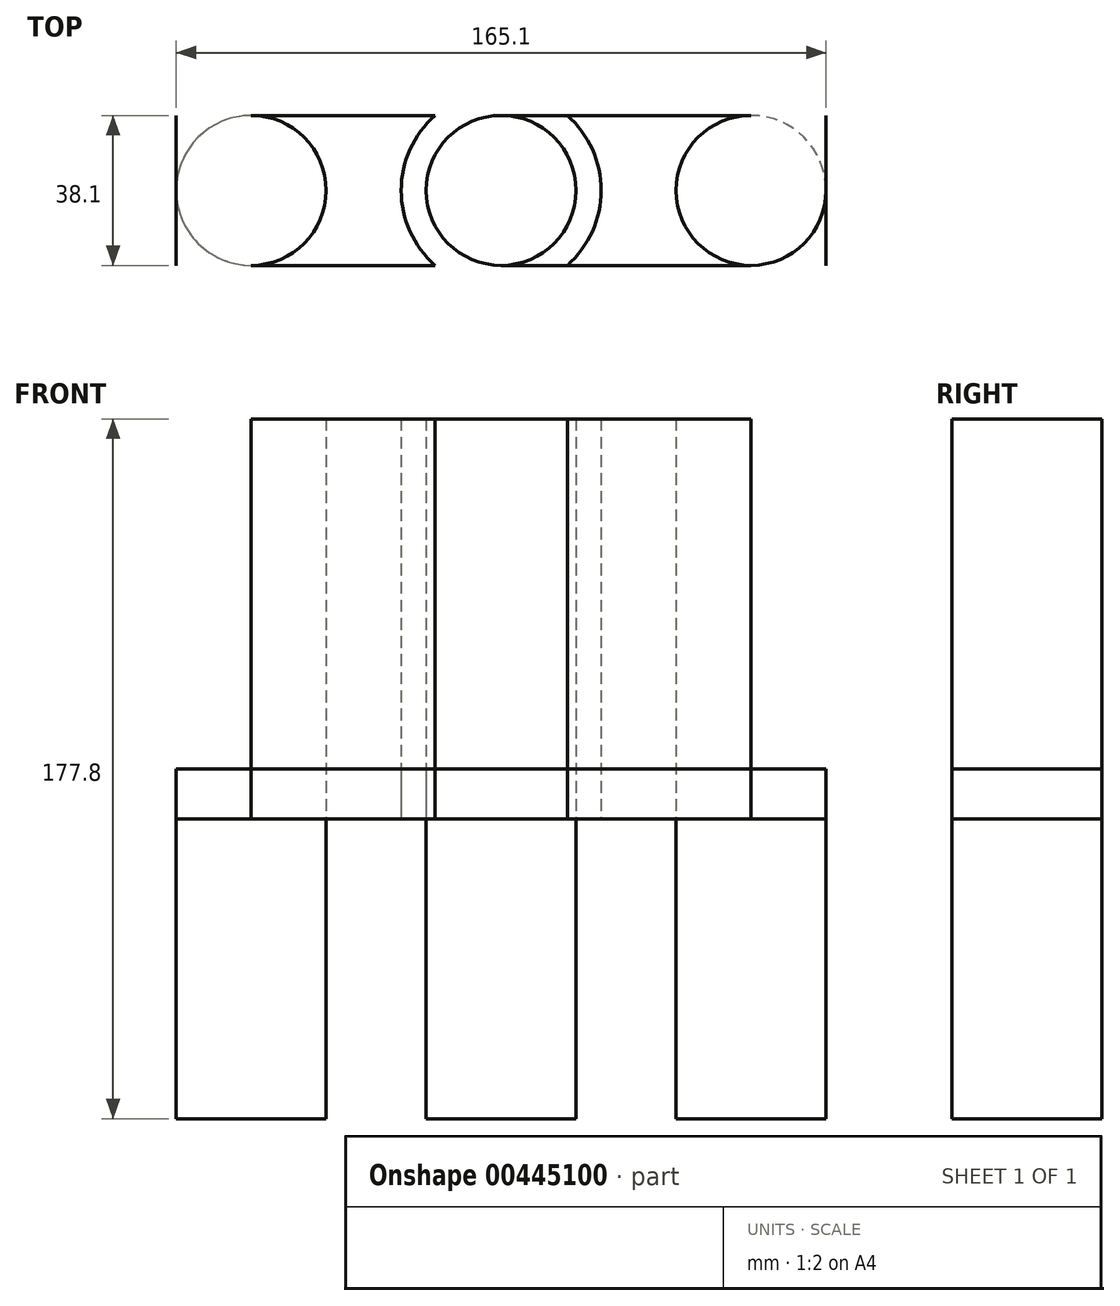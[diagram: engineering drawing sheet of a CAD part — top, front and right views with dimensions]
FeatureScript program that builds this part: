
annotation { "Feature Type Name" : "Feature", "Feature Type Description" : "" }
export const myFeature = defineFeature(function(context is Context, id is Id, definition is map)
    precondition{}
    {
        {
            var Q0;
            Q0=qCreatedBy(makeId("Top.planeOp"),FACE);
            var sketch = newSketch(context, id + "F0", { "sketchPlane" : qUnion([Q0])});
            skLineSegment(sketch, "E0.bottom", {"start": v(82.55, 19.05) * mm, "end": v(-82.55, 19.05) * mm});
            skLineSegment(sketch, "E0.top", {"start": v(82.55, -19.05) * mm, "end": v(-82.55, -19.05) * mm});
            skLineSegment(sketch, "E0.left", {"start": v(82.55, 19.05) * mm, "end": v(82.55, -19.05) * mm});
            skLineSegment(sketch, "E0.right", {"start": v(-82.55, 19.05) * mm, "end": v(-82.55, -19.05) * mm});
            skPoint(sketch, "E0.middle", {"position": v(0, 0) * mm});
            skCircle(sketch, "E1", {"center": v(0, 0) * mm, "radius": 25.4 * mm});
            skCircle(sketch, "E2", {"center": v(0, 0) * mm, "radius": 19.05 * mm});
            skLineSegment(sketch, "E3", {"start": v(-19.05, 0) * mm, "end": v(-44.45, 0) * mm});
            skLineSegment(sketch, "E4", {"start": v(19.05, 0) * mm, "end": v(44.45, 0) * mm});
            skCircle(sketch, "E5", {"center": v(-63.5, 0) * mm, "radius": 19.05 * mm});
            skCircle(sketch, "E6", {"center": v(63.5, 0) * mm, "radius": 19.05 * mm});
            skSolve(sketch);
        }
        {
            var Q0;
            {var subQ0=sQuery(id+"F0.wireOp",EDGE,"E0.right");Q0=makeQuery(id+"F0.imprint","IMPRINT",FACE,{"disambiguationData":[TD([[makeQuery(id+"F0.imprint","IMPRINT",EDGE,{"derivedFrom":subQ0}),1.0]])]});}
            var Q1;
            {var subQ0=sQuery(id+"F0.wireOp",EDGE,"E0.left");Q1=makeQuery(id+"F0.imprint","IMPRINT",FACE,{"disambiguationData":[TD([[makeQuery(id+"F0.imprint","IMPRINT",EDGE,{"derivedFrom":subQ0}),-1.0]])]});}
            var Q2;
            {var subQ0=sQuery(id+"F0.wireOp",EDGE,"E1");var subQ1=sQuery(id+"F0.wireOp",EDGE,"E0.bottom");var subQ2=makeQuery(id+"F0.imprint","INTERSECT",VERTEX,{"disambiguationData":[OD(0.0)],"derivedFrom":[subQ1,subQ0]});Q2=makeQuery(id+"F0.imprint","IMPRINT",FACE,{"disambiguationData":[TD([[makeQuery(id+"F0.imprint","IMPRINT",EDGE,{"disambiguationData":[TD([[subQ2,-1.0]])],"derivedFrom":subQ1}),1.0]])]});}
            var Q3;
            {var subQ0=sQuery(id+"F0.wireOp",EDGE,"E2");var subQ1=makeQuery(id+"F0.imprint","INTERSECT",VERTEX,{"derivedFrom":[subQ0,sQuery(id+"F0.wireOp",EDGE,"E4")]});Q3=makeQuery(id+"F0.imprint","IMPRINT",FACE,{"disambiguationData":[TD([[makeQuery(id+"F0.imprint","IMPRINT",EDGE,{"disambiguationData":[TD([[subQ1,-1.0]])],"derivedFrom":subQ0}),1.0]])]});}
            var Q4;
            {var subQ0=sQuery(id+"F0.wireOp",EDGE,"E1");var subQ1=sQuery(id+"F0.wireOp",EDGE,"E0.bottom");var subQ2=makeQuery(id+"F0.imprint","INTERSECT",VERTEX,{"disambiguationData":[OD(1.0)],"derivedFrom":[subQ1,subQ0]});Q4=makeQuery(id+"F0.imprint","IMPRINT",FACE,{"disambiguationData":[TD([[makeQuery(id+"F0.imprint","IMPRINT",EDGE,{"disambiguationData":[TD([[subQ2,-1.0]])],"derivedFrom":subQ1}),1.0]])]});}
            var Q5;
            {var subQ0=sQuery(id+"F0.wireOp",EDGE,"E5");var subQ1=makeQuery(id+"F0.imprint","INTERSECT",VERTEX,{"derivedFrom":[sQuery(id+"F0.wireOp",EDGE,"E3"),subQ0]});Q5=makeQuery(id+"F0.imprint","IMPRINT",FACE,{"disambiguationData":[TD([[makeQuery(id+"F0.imprint","IMPRINT",EDGE,{"disambiguationData":[TD([[subQ1,-1.0]])],"derivedFrom":subQ0}),1.0]])]});}
            var Q6;
            {var subQ0=sQuery(id+"F0.wireOp",EDGE,"E1");var subQ1=sQuery(id+"F0.wireOp",EDGE,"E0.top");var subQ2=makeQuery(id+"F0.imprint","INTERSECT",VERTEX,{"disambiguationData":[OD(1.0)],"derivedFrom":[subQ1,subQ0]});Q6=makeQuery(id+"F0.imprint","IMPRINT",FACE,{"disambiguationData":[TD([[makeQuery(id+"F0.imprint","IMPRINT",EDGE,{"disambiguationData":[TD([[subQ2,-1.0]])],"derivedFrom":subQ1}),-1.0]])]});}
            var Q7;
            {var subQ0=sQuery(id+"F0.wireOp",EDGE,"E1");var subQ1=sQuery(id+"F0.wireOp",EDGE,"E0.bottom");var subQ2=makeQuery(id+"F0.imprint","INTERSECT",VERTEX,{"disambiguationData":[OD(1.0)],"derivedFrom":[subQ1,subQ0]});Q7=makeQuery(id+"F0.imprint","IMPRINT",FACE,{"disambiguationData":[TD([[makeQuery(id+"F0.imprint","IMPRINT",EDGE,{"disambiguationData":[TD([[subQ2,1.0]])],"derivedFrom":subQ1}),1.0]])]});}
            var Q8;
            {var subQ0=sQuery(id+"F0.wireOp",EDGE,"E1");var subQ1=sQuery(id+"F0.wireOp",EDGE,"E0.top");var subQ2=makeQuery(id+"F0.imprint","INTERSECT",VERTEX,{"disambiguationData":[OD(1.0)],"derivedFrom":[subQ1,subQ0]});Q8=makeQuery(id+"F0.imprint","IMPRINT",FACE,{"disambiguationData":[TD([[makeQuery(id+"F0.imprint","IMPRINT",EDGE,{"disambiguationData":[TD([[subQ2,1.0]])],"derivedFrom":subQ1}),-1.0]])]});}
            var Q9;
            {var subQ0=sQuery(id+"F0.wireOp",EDGE,"E1");var subQ1=sQuery(id+"F0.wireOp",EDGE,"E0.top");var subQ2=makeQuery(id+"F0.imprint","INTERSECT",VERTEX,{"disambiguationData":[OD(0.0)],"derivedFrom":[subQ1,subQ0]});Q9=makeQuery(id+"F0.imprint","IMPRINT",FACE,{"disambiguationData":[TD([[makeQuery(id+"F0.imprint","IMPRINT",EDGE,{"disambiguationData":[TD([[subQ2,-1.0]])],"derivedFrom":subQ1}),-1.0]])]});}
            var Q10;
            {var subQ0=sQuery(id+"F0.wireOp",EDGE,"E6");var subQ1=sQuery(id+"F0.wireOp",EDGE,"E0.top");var subQ2=makeQuery(id+"F0.imprint","INTERSECT",VERTEX,{"derivedFrom":[subQ1,subQ0]});Q10=makeQuery(id+"F0.imprint","IMPRINT",FACE,{"disambiguationData":[TD([[makeQuery(id+"F0.imprint","IMPRINT",EDGE,{"disambiguationData":[TD([[subQ2,-1.0]])],"derivedFrom":subQ1}),-1.0]])]});}
            var Q11;
            {var subQ0=sQuery(id+"F0.wireOp",EDGE,"E6");var subQ1=sQuery(id+"F0.wireOp",EDGE,"E0.bottom");var subQ2=makeQuery(id+"F0.imprint","INTERSECT",VERTEX,{"derivedFrom":[subQ1,subQ0]});Q11=makeQuery(id+"F0.imprint","IMPRINT",FACE,{"disambiguationData":[TD([[makeQuery(id+"F0.imprint","IMPRINT",EDGE,{"disambiguationData":[TD([[subQ2,-1.0]])],"derivedFrom":subQ1}),1.0]])]});}
            var Q12;
            {var subQ0=sQuery(id+"F0.wireOp",EDGE,"E6");var subQ1=makeQuery(id+"F0.imprint","INTERSECT",VERTEX,{"derivedFrom":[sQuery(id+"F0.wireOp",EDGE,"E0.bottom"),subQ0]});Q12=makeQuery(id+"F0.imprint","IMPRINT",FACE,{"disambiguationData":[TD([[makeQuery(id+"F0.imprint","IMPRINT",EDGE,{"disambiguationData":[TD([[subQ1,1.0]])],"derivedFrom":subQ0}),1.0]])]});}
            extrude(context, id + "F1", {"entities" : qUnion([Q0, Q1, Q2, Q3, Q4, Q5, Q6, Q7, Q8, Q9, Q10, Q11, Q12]), "depth" : 12.7 * mm});
        }
        {
            var Q0;
            {var subQ0=sQuery(id+"F0.wireOp",EDGE,"E6");var subQ1=makeQuery(id+"F0.imprint","INTERSECT",VERTEX,{"derivedFrom":[sQuery(id+"F0.wireOp",EDGE,"E0.bottom"),subQ0]});Q0=makeQuery(id+"F0.imprint","IMPRINT",FACE,{"disambiguationData":[TD([[makeQuery(id+"F0.imprint","IMPRINT",EDGE,{"disambiguationData":[TD([[subQ1,1.0]])],"derivedFrom":subQ0}),1.0]])]});}
            var Q1;
            {var subQ0=sQuery(id+"F0.wireOp",EDGE,"E2");var subQ1=makeQuery(id+"F0.imprint","INTERSECT",VERTEX,{"derivedFrom":[subQ0,sQuery(id+"F0.wireOp",EDGE,"E4")]});Q1=makeQuery(id+"F0.imprint","IMPRINT",FACE,{"disambiguationData":[TD([[makeQuery(id+"F0.imprint","IMPRINT",EDGE,{"disambiguationData":[TD([[subQ1,-1.0]])],"derivedFrom":subQ0}),1.0]])]});}
            var Q2;
            {var subQ0=sQuery(id+"F0.wireOp",EDGE,"E5");var subQ1=makeQuery(id+"F0.imprint","INTERSECT",VERTEX,{"derivedFrom":[sQuery(id+"F0.wireOp",EDGE,"E3"),subQ0]});Q2=makeQuery(id+"F0.imprint","IMPRINT",FACE,{"disambiguationData":[TD([[makeQuery(id+"F0.imprint","IMPRINT",EDGE,{"disambiguationData":[TD([[subQ1,-1.0]])],"derivedFrom":subQ0}),1.0]])]});}
            extrude(context, id + "F2", {"entities" : qUnion([Q0, Q1, Q2]), "oppositeDirection" : true, "depth" : 76.2 * mm});
        }
        {
            var Q0;
            {var subQ0=sQuery(id+"F0.wireOp",EDGE,"E1");var subQ1=sQuery(id+"F0.wireOp",EDGE,"E0.bottom");var subQ2=makeQuery(id+"F0.imprint","INTERSECT",VERTEX,{"disambiguationData":[OD(0.0)],"derivedFrom":[subQ1,subQ0]});Q0=makeQuery(id+"F0.imprint","IMPRINT",FACE,{"disambiguationData":[TD([[makeQuery(id+"F0.imprint","IMPRINT",EDGE,{"disambiguationData":[TD([[subQ2,-1.0]])],"derivedFrom":subQ1}),-1.0]])]});}
            var Q1;
            {var subQ0=sQuery(id+"F0.wireOp",EDGE,"E1");var subQ1=sQuery(id+"F0.wireOp",EDGE,"E0.bottom");var subQ2=makeQuery(id+"F0.imprint","INTERSECT",VERTEX,{"disambiguationData":[OD(1.0)],"derivedFrom":[subQ1,subQ0]});Q1=makeQuery(id+"F0.imprint","IMPRINT",FACE,{"disambiguationData":[TD([[makeQuery(id+"F0.imprint","IMPRINT",EDGE,{"disambiguationData":[TD([[subQ2,1.0]])],"derivedFrom":subQ1}),1.0]])]});}
            var Q2;
            {var subQ0=sQuery(id+"F0.wireOp",EDGE,"E2");var subQ1=makeQuery(id+"F0.imprint","INTERSECT",VERTEX,{"derivedFrom":[subQ0,sQuery(id+"F0.wireOp",EDGE,"E4")]});Q2=makeQuery(id+"F0.imprint","IMPRINT",FACE,{"disambiguationData":[TD([[makeQuery(id+"F0.imprint","IMPRINT",EDGE,{"disambiguationData":[TD([[subQ1,-1.0]])],"derivedFrom":subQ0}),1.0]])]});}
            var Q3;
            {var subQ0=sQuery(id+"F0.wireOp",EDGE,"E1");var subQ1=sQuery(id+"F0.wireOp",EDGE,"E0.top");var subQ2=makeQuery(id+"F0.imprint","INTERSECT",VERTEX,{"disambiguationData":[OD(1.0)],"derivedFrom":[subQ1,subQ0]});Q3=makeQuery(id+"F0.imprint","IMPRINT",FACE,{"disambiguationData":[TD([[makeQuery(id+"F0.imprint","IMPRINT",EDGE,{"disambiguationData":[TD([[subQ2,1.0]])],"derivedFrom":subQ1}),-1.0]])]});}
            var Q4;
            {var subQ0=sQuery(id+"F0.wireOp",EDGE,"E1");var subQ1=sQuery(id+"F0.wireOp",EDGE,"E0.top");var subQ2=makeQuery(id+"F0.imprint","INTERSECT",VERTEX,{"disambiguationData":[OD(0.0)],"derivedFrom":[subQ1,subQ0]});Q4=makeQuery(id+"F0.imprint","IMPRINT",FACE,{"disambiguationData":[TD([[makeQuery(id+"F0.imprint","IMPRINT",EDGE,{"disambiguationData":[TD([[subQ2,-1.0]])],"derivedFrom":subQ1}),1.0]])]});}
            var Q5;
            {var subQ0=sQuery(id+"F0.wireOp",EDGE,"E1");var subQ1=sQuery(id+"F0.wireOp",EDGE,"E0.top");var subQ2=makeQuery(id+"F0.imprint","INTERSECT",VERTEX,{"disambiguationData":[OD(0.0)],"derivedFrom":[subQ1,subQ0]});Q5=makeQuery(id+"F0.imprint","IMPRINT",FACE,{"disambiguationData":[TD([[makeQuery(id+"F0.imprint","IMPRINT",EDGE,{"disambiguationData":[TD([[subQ2,-1.0]])],"derivedFrom":subQ1}),-1.0]])]});}
            var Q6;
            {var subQ0=sQuery(id+"F0.wireOp",EDGE,"E1");var subQ1=sQuery(id+"F0.wireOp",EDGE,"E0.bottom");var subQ2=makeQuery(id+"F0.imprint","INTERSECT",VERTEX,{"disambiguationData":[OD(0.0)],"derivedFrom":[subQ1,subQ0]});Q6=makeQuery(id+"F0.imprint","IMPRINT",FACE,{"disambiguationData":[TD([[makeQuery(id+"F0.imprint","IMPRINT",EDGE,{"disambiguationData":[TD([[subQ2,-1.0]])],"derivedFrom":subQ1}),1.0]])]});}
            extrude(context, id + "F3", {"entities" : qUnion([Q0, Q1, Q2, Q3, Q4, Q5, Q6]), "depth" : 101.6 * mm});
        }
    });
